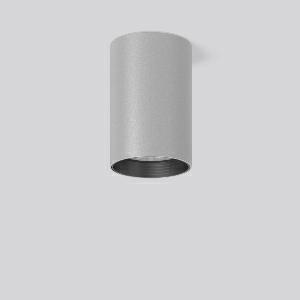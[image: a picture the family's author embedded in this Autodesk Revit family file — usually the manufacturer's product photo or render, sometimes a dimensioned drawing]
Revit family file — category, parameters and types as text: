
# Revit family: heledon_maxi_a_931227_004_3_e2a6
name_source: partatom
category: Lighting Fixtures
units: mm (PartAtom-declared; Revit-internal decimal feet)

## family parameters
Cut with Voids When Loaded = No
Host = Face
Light Source = No
Part Type = Normal
Room Calculation Point = No
Round Connector Dimension = Use Diameter
Shared = No

## types (1)
- HELEDON maxi A (1 x LED Modul 935, 3750 lm, 3500)
    Apparent Load = 35 VA
    Approval mark = CE
    CIE Flux Codes = 97 100 100 100 100
    Color Rendering = 92
    Color Temperature = 3500
    Default Elevation = 1800 mm
    Description = Series: HELEDON maxi
Cylindrical surface-mounted downlight. Housing: die-cast aluminium, powder-coated. Internal ceiling frame polycarbonate with bayonet mounting. Black plastic ring and recessed LED to prevent glare from the side. Optical assembly with lens made of plastic (polycarbonate) for the best homogeneous light distribution - can be changed without tools. Best colour rendering index Ra>90. Suitable for Ceiling mounting. Easy installation with a separate ceiling frame with bayonet mounting and plug connection. Driver integrated. Connected via plug-in connector. High quality converter without flickering and stroboscopic effect. The following accessories can be mounted without use of tools: interchangeable lenses, decorative glasses, honeycomb louvre, clear and frosted diffusers, white interchangeable plastic ring. 
Colour: silver
Diameter: 123 mm
Height: 183 mm
Lamp: LED
Socket: without socket
Colour temperature: 3500K
Colour rendering index (CRI): 92
System power: 35 W
Rated luminous flux: 3750 lm
Luminous efficiency: 107 lm/W
Control gear: Regulated power supply
Protection class: I
Type of protection: IP 20
    Height = 183 mm
    Lamp = 1 x LED Modul 935
    Lamp Light Flux = 3750 lm
    Lamp count = 1
    Length = 123 mm
    Lifetime = 50000 h
    Luminous efficacy = 107 lm/W
    Manufacturer = RZB
    ModVariant = No
    Model = 931227.004.3
    Mounting Place = Ceiling
    Mounting Type = Surface mounted
    Number of Poles = 1
    OnlyDefault = Yes
    Power Factor = 1
    Product Name = HELEDON maxi A
    Product group = Surface mounted downlights
    ProductGroupID = 302
    Protection Class = Protection class I
    Protection Degree = IP 20
    RLX_Detail_Level = 1
    RLX_Emergency_Light_Flux = 0 lm
    RLX_Emergency_Type = 0
    RLX_Emergency_Type_DB = No
    RlxData = <blob elided: 100137 chars, md5=ca84aa01>
    Socket = socket
    Standby Power = 0 W
    System Light Flux = 3750 lm
    System Power = 35 W
    Type Comments = Product without accessories
    Type Image = 931193.004.jpg
    URL = http://relux.com
    VarID = ---
    Voltage = 230 V
    Voltage Range = 220-240 V
    Weight = 0.00 kg
    Width = 0 mm  [stored 0 ft]

note: [stored X ft] marks values corroborated as IEEE doubles in the binary element streams (Revit-internal decimal feet)

## geometry (parser evidence)
native form markers: Blend x4, Sweep x11
no freeform markers — native parametric forms only
